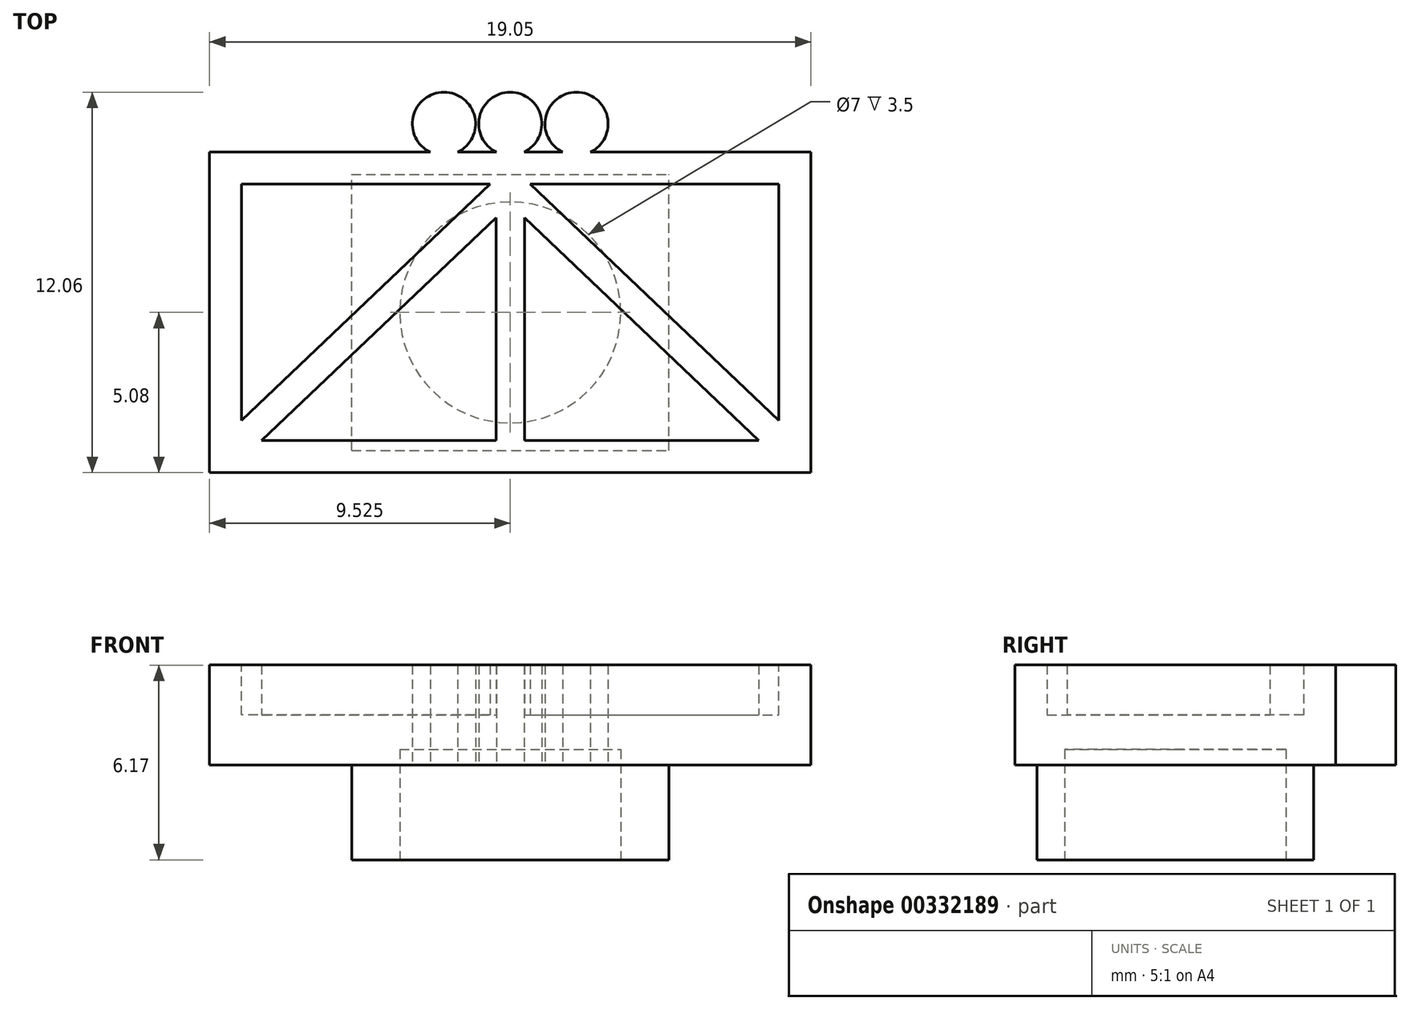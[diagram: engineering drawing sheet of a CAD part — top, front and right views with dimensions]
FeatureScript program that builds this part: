
annotation { "Feature Type Name" : "Feature", "Feature Type Description" : "" }
export const myFeature = defineFeature(function(context is Context, id is Id, definition is map)
    precondition{}
    {
        {
            var Q0;
            Q0=qCreatedBy(makeId("Top.planeOp"),FACE);
            var sketch = newSketch(context, id + "F0", { "sketchPlane" : qUnion([Q0])});
            skLineSegment(sketch, "E0.bottom", {"start": v(-19.05, 10.16) * mm, "end": v(0, 10.16) * mm});
            skLineSegment(sketch, "E0.top", {"start": v(-19.05, 0) * mm, "end": v(0, 0) * mm});
            skLineSegment(sketch, "E0.left", {"start": v(-19.05, 10.16) * mm, "end": v(-19.05, 0) * mm});
            skLineSegment(sketch, "E0.right", {"start": v(0, 10.16) * mm, "end": v(0, 0) * mm});
            skCircle(sketch, "E1", {"center": v(-9.53, 11.06) * mm, "radius": 1 * mm});
            skLineSegment(sketch, "E2", {"start": v(-9.52, 10.16) * mm, "end": v(-9.52, 0) * mm, "construction": true});
            skCircle(sketch, "E3", {"center": v(-11.62, 11.06) * mm, "radius": 1 * mm});
            skCircle(sketch, "E4.MirrorC", {"center": v(-7.43, 11.06) * mm, "radius": 1 * mm});
            skSolve(sketch);
        }
        {
            var Q0;
            Q0=qSketchRegion(id+"F0",true);
            extrude(context, id + "F1", {"entities" : qUnion([Q0]), "depth" : 3.17 * mm});
        }
        {
            var Q0;
            Q0=makeQuery(id+"F1.opExtrude","CAP_FACE",FACE,{"disambiguationData":[OSD([sQuery(id+"F0.wireOp",EDGE,"E0.bottom"),sQuery(id+"F0.wireOp",EDGE,"E0.top"),sQuery(id+"F0.wireOp",EDGE,"E0.left"),sQuery(id+"F0.wireOp",EDGE,"E0.right")])],"isStart":false});
            var sketch = newSketch(context, id + "F2", { "sketchPlane" : qUnion([Q0])});
            skLineSegment(sketch, "E5.bottom", {"start": v(-18.03, 9.14) * mm, "end": v(-1.02, 9.14) * mm});
            skLineSegment(sketch, "E5.top", {"start": v(-18.03, 1.02) * mm, "end": v(-1.02, 1.02) * mm});
            skLineSegment(sketch, "E5.left", {"start": v(-18.03, 9.14) * mm, "end": v(-18.03, 1.02) * mm});
            skLineSegment(sketch, "E5.right", {"start": v(-1.02, 9.14) * mm, "end": v(-1.02, 1.02) * mm});
            skSolve(sketch);
        }
        {
            var Q0;
            Q0=qSketchRegion(id+"F2",true);
            extrude(context, id + "F3", {"entities" : qUnion([Q0]), "operationType" : NewBodyOperationType.REMOVE, "oppositeDirection" : true, "depth" : 1.59 * mm});
        }
        {
            var Q0;
            Q0=makeQuery(id+"F3.boolean.opBoolean","COPY",FACE,{"derivedFrom":makeQuery(id+"F3.opExtrude","CAP_FACE",FACE,{"disambiguationData":[OSD([sQuery(id+"F2.wireOp",EDGE,"E5.bottom"),sQuery(id+"F2.wireOp",EDGE,"E5.top"),sQuery(id+"F2.wireOp",EDGE,"E5.left"),sQuery(id+"F2.wireOp",EDGE,"E5.right")])],"isStart":false})});
            var sketch = newSketch(context, id + "F4", { "sketchPlane" : qUnion([Q0])});
            skLineSegment(sketch, "E6", {"start": v(-9.53, 9.14) * mm, "end": v(-10.16, 9.14) * mm});
            skLineSegment(sketch, "E7", {"start": v(-9.53, 9.14) * mm, "end": v(-9.52, 1.02) * mm, "construction": true});
            skLineSegment(sketch, "E8", {"start": v(-18.03, 1.65) * mm, "end": v(-18.03, 1.02) * mm});
            skLineSegment(sketch, "E9", {"start": v(-18.03, 1.02) * mm, "end": v(-17.4, 1.02) * mm});
            skLineSegment(sketch, "E10", {"start": v(-17.4, 1.02) * mm, "end": v(-9.52, 8.5) * mm});
            skLineSegment(sketch, "E11", {"start": v(-9.52, 8.5) * mm, "end": v(-9.52, 9.14) * mm});
            skLineSegment(sketch, "E12", {"start": v(-10.16, 9.14) * mm, "end": v(-18.03, 1.65) * mm});
            skLineSegment(sketch, "E13.MirrorCS", {"start": v(-1.65, 1.02) * mm, "end": v(-9.53, 8.5) * mm});
            skLineSegment(sketch, "E14.MirrorCS", {"start": v(-8.89, 9.14) * mm, "end": v(-1.02, 1.65) * mm});
            skLineSegment(sketch, "E15.MirrorCS", {"start": v(-9.52, 9.14) * mm, "end": v(-8.89, 9.14) * mm});
            skLineSegment(sketch, "E16.MirrorCS", {"start": v(-1.02, 1.02) * mm, "end": v(-1.65, 1.02) * mm});
            skLineSegment(sketch, "E17.MirrorCS", {"start": v(-1.02, 1.65) * mm, "end": v(-1.02, 1.02) * mm});
            skLineSegment(sketch, "E18", {"start": v(-9.83, 8.22) * mm, "end": v(-9.83, 1.02) * mm});
            skLineSegment(sketch, "E19", {"start": v(-9.83, 1.02) * mm, "end": v(-9.52, 1.02) * mm});
            skLineSegment(sketch, "E20.MirrorCS", {"start": v(-9.23, 8.22) * mm, "end": v(-9.23, 1.02) * mm});
            skLineSegment(sketch, "E21", {"start": v(-9.83, 8.22) * mm, "end": v(-9.52, 8.5) * mm});
            skSolve(sketch);
        }
        {
            var Q0;
            Q0=qSketchRegion(id+"F4",true);
            var Q1;
            Q1=makeQuery(id+"F1.opExtrude","CAP_FACE",FACE,{"disambiguationData":[OSD([sQuery(id+"F0.wireOp",EDGE,"E0.bottom"),sQuery(id+"F0.wireOp",EDGE,"E0.top"),sQuery(id+"F0.wireOp",EDGE,"E0.left"),sQuery(id+"F0.wireOp",EDGE,"E0.right"),sQuery(id+"F0.wireOp",EDGE,"XctMcTzM-jzK6-gSmv-2nxO-Hmrl2WoydrkH.bottom"),sQuery(id+"F0.wireOp",EDGE,"XctMcTzM-jzK6-gSmv-2nxO-Hmrl2WoydrkH.left"),sQuery(id+"F0.wireOp",EDGE,"XctMcTzM-jzK6-gSmv-2nxO-Hmrl2WoydrkH.right")])],"isStart":false});
            extrude(context, id + "F5", {"entities" : qUnion([Q0]), "operationType" : NewBodyOperationType.ADD, "endBound" : BoundingType.UP_TO_SURFACE, "endBoundEntityFace" : qUnion([Q1]), "depth" : 25.4 * mm});
        }
        {
            var Q0;
            Q0=makeQuery(id+"F1.opExtrude","CAP_FACE",FACE,{"disambiguationData":[OSD([sQuery(id+"F0.wireOp",EDGE,"E0.bottom"),sQuery(id+"F0.wireOp",EDGE,"E0.top"),sQuery(id+"F0.wireOp",EDGE,"E0.left"),sQuery(id+"F0.wireOp",EDGE,"E0.right"),sQuery(id+"F0.wireOp",EDGE,"E1"),sQuery(id+"F0.wireOp",EDGE,"E3"),sQuery(id+"F0.wireOp",EDGE,"E4.MirrorC")])],"isStart":true});
            var sketch = newSketch(context, id + "F6", { "sketchPlane" : qUnion([Q0])});
            skLineSegment(sketch, "E22.bottom", {"start": v(-14.55, -0.7) * mm, "end": v(-4.5, -0.7) * mm});
            skLineSegment(sketch, "E22.top", {"start": v(-14.55, -9.46) * mm, "end": v(-4.5, -9.46) * mm});
            skLineSegment(sketch, "E22.left", {"start": v(-14.55, -0.7) * mm, "end": v(-14.55, -9.46) * mm});
            skLineSegment(sketch, "E22.right", {"start": v(-4.5, -0.7) * mm, "end": v(-4.5, -9.46) * mm});
            skSolve(sketch);
        }
        {
            var Q0;
            Q0=qSketchRegion(id+"F6",true);
            extrude(context, id + "F7", {"entities" : qUnion([Q0]), "operationType" : NewBodyOperationType.ADD, "depth" : 3 * mm, "offsetDistance" : 25 * mm});
        }
        {
            var Q0;
            Q0=makeQuery(id+"F7.opExtrude","CAP_FACE",FACE,{"disambiguationData":[OSD([sQuery(id+"F6.wireOp",EDGE,"E22.bottom"),sQuery(id+"F6.wireOp",EDGE,"E22.top"),sQuery(id+"F6.wireOp",EDGE,"E22.left"),sQuery(id+"F6.wireOp",EDGE,"E22.right")])],"isStart":false});
            var sketch = newSketch(context, id + "F8", { "sketchPlane" : qUnion([Q0])});
            skCircle(sketch, "E23", {"center": v(-9.52, -5.08) * mm, "radius": 3.5 * mm});
            skLineSegment(sketch, "E24", {"start": v(-19.05, -5.08) * mm, "end": v(0, -5.08) * mm, "construction": true});
            skPoint(sketch, "E24.endSnap0", {"position": v(-4.5, -5.08) * mm});
            skLineSegment(sketch, "E25", {"start": v(-9.53, 0) * mm, "end": v(-9.53, -9.46) * mm, "construction": true});
            skSolve(sketch);
        }
        {
            var Q0;
            Q0=makeQuery(id+"F8.imprint","IMPRINT",FACE,{"disambiguationData":[TD([[makeQuery(id+"F8.imprint","IMPRINT",EDGE,{"derivedFrom":sQuery(id+"F8.wireOp",EDGE,"E23")}),1.0]])]});
            extrude(context, id + "F9", {"entities" : qUnion([Q0]), "operationType" : NewBodyOperationType.REMOVE, "oppositeDirection" : true, "depth" : 3.5 * mm, "offsetDistance" : 25 * mm});
        }
        {
            var Q0;
            {var subQ0=sQuery(id+"F2.wireOp",EDGE,"E5.top");Q0=makeQuery(id+"F5.boolean.opBoolean","SPLIT",FACE,{"disambiguationData":[TD([makeQuery(id+"F3.boolean.opBoolean","COPY",FACE,{"derivedFrom":makeQuery(id+"F3.opExtrude","SWEPT_FACE",FACE,{"disambiguationData":[OSD([subQ0])]})})])],"derivedFrom":makeQuery(id+"F3.boolean.opBoolean","COPY",FACE,{"derivedFrom":makeQuery(id+"F3.opExtrude","CAP_FACE",FACE,{"disambiguationData":[OSD([sQuery(id+"F2.wireOp",EDGE,"E5.bottom"),subQ0,sQuery(id+"F2.wireOp",EDGE,"E5.left"),sQuery(id+"F2.wireOp",EDGE,"E5.right")])],"isStart":false})})});}
            var sketch = newSketch(context, id + "F10", { "sketchPlane" : qUnion([Q0])});
            skLineSegment(sketch, "E26", {"start": v(-9.98, 8.08) * mm, "end": v(-9.98, 1.02) * mm});
            skLineSegment(sketch, "E27", {"start": v(-9.98, 1.02) * mm, "end": v(-9.52, 1.02) * mm});
            skLineSegment(sketch, "E28", {"start": v(-9.98, 8.08) * mm, "end": v(-9.52, 8.5) * mm});
            skLineSegment(sketch, "E29", {"start": v(-9.07, 8.08) * mm, "end": v(-9.07, 1.02) * mm});
            skLineSegment(sketch, "E30", {"start": v(-9.07, 1.02) * mm, "end": v(-9.52, 1.02) * mm});
            skLineSegment(sketch, "E31", {"start": v(-9.53, 8.5) * mm, "end": v(-9.07, 8.08) * mm});
            skSolve(sketch);
        }
        {
            var Q0;
            Q0 = qSketchRegion(id + "F10", true);
            var Q1;
            Q1=makeQuery(id+"F5.boolean.opBoolean","MERGE",FACE,{"derivedFrom":[makeQuery(id+"F1.opExtrude","CAP_FACE",FACE,{"disambiguationData":[OSD([sQuery(id+"F0.wireOp",EDGE,"E0.bottom"),sQuery(id+"F0.wireOp",EDGE,"E0.top"),sQuery(id+"F0.wireOp",EDGE,"E0.left"),sQuery(id+"F0.wireOp",EDGE,"E0.right"),sQuery(id+"F0.wireOp",EDGE,"E1"),sQuery(id+"F0.wireOp",EDGE,"E3"),sQuery(id+"F0.wireOp",EDGE,"E4.MirrorC")])],"isStart":false}),makeQuery(id+"F5.opExtrude","CAP_FACE",FACE,{"disambiguationData":[OSD([sQuery(id+"F4.wireOp",EDGE,"E6"),sQuery(id+"F4.wireOp",EDGE,"E8"),sQuery(id+"F4.wireOp",EDGE,"E9"),sQuery(id+"F4.wireOp",EDGE,"E10"),sQuery(id+"F4.wireOp",EDGE,"E12"),sQuery(id+"F4.wireOp",EDGE,"E13.MirrorCS"),sQuery(id+"F4.wireOp",EDGE,"E14.MirrorCS"),sQuery(id+"F4.wireOp",EDGE,"E15.MirrorCS"),sQuery(id+"F4.wireOp",EDGE,"E16.MirrorCS"),sQuery(id+"F4.wireOp",EDGE,"E17.MirrorCS"),sQuery(id+"F4.wireOp",EDGE,"E21")])],"isStart":false})]});
            extrude(context, id + "F11", {"entities" : qUnion([Q0]), "operationType" : NewBodyOperationType.ADD, "endBound" : BoundingType.UP_TO_SURFACE, "depth" : 25 * mm, "endBoundEntityFace" : qUnion([Q1]), "offsetDistance" : 25 * mm});
        }
    });
